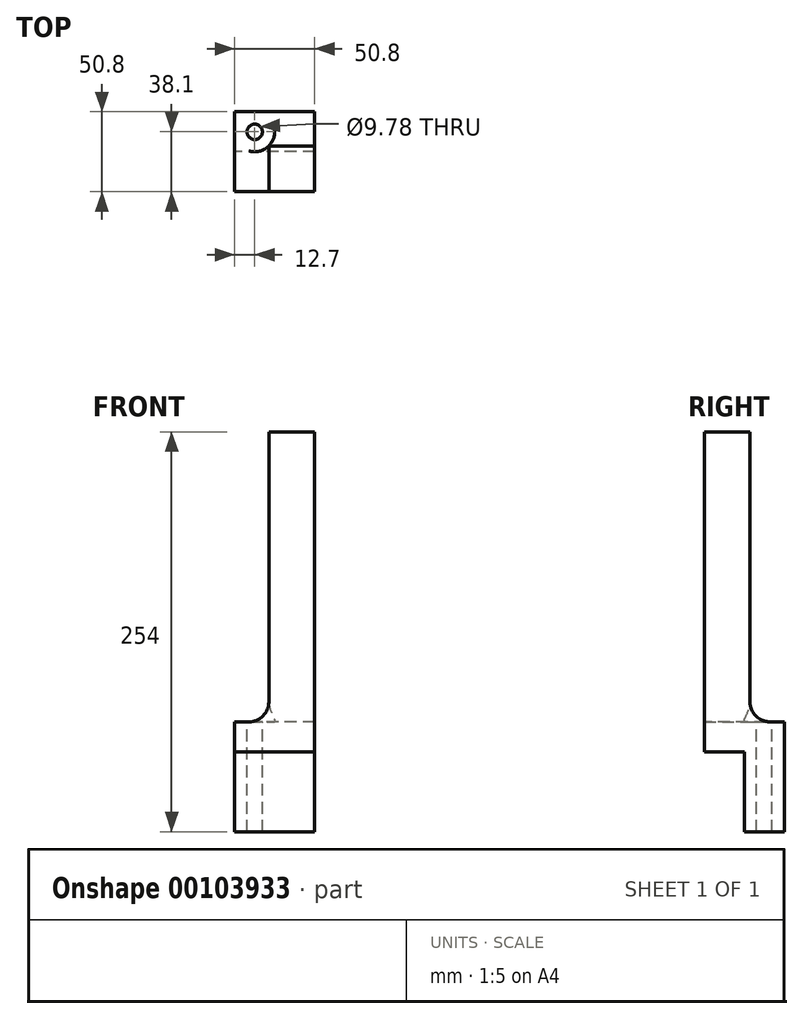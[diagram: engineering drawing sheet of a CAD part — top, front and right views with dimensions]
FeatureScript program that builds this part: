
annotation { "Feature Type Name" : "Feature", "Feature Type Description" : "" }
export const myFeature = defineFeature(function(context is Context, id is Id, definition is map)
    precondition{}
    {
        {
            var Q0;
            Q0=qCreatedBy(makeId("Top.planeOp"),FACE);
            var sketch = newSketch(context, id + "F0", { "sketchPlane" : qUnion([Q0])});
            skLineSegment(sketch, "E0.bottom", {"start": v(0, 0) * mm, "end": v(-50.8, 0) * mm});
            skLineSegment(sketch, "E0.top", {"start": v(0, 50.8) * mm, "end": v(-50.8, 50.8) * mm});
            skLineSegment(sketch, "E0.left", {"start": v(0, 0) * mm, "end": v(0, 50.8) * mm});
            skLineSegment(sketch, "E0.right", {"start": v(-50.8, 0) * mm, "end": v(-50.8, 50.8) * mm});
            skSolve(sketch);
        }
        {
            var Q0;
            Q0=qSketchRegion(id+"F0",true);
            extrude(context, id + "F1", {"entities" : qUnion([Q0]), "depth" : 254 * mm});
        }
        {
            var Q0;
            Q0=makeQuery(id+"F1.opExtrude","SWEPT_FACE",FACE,{"disambiguationData":[OSD([sQuery(id+"F0.wireOp",EDGE,"E0.right")])]});
            var sketch = newSketch(context, id + "F2", { "sketchPlane" : qUnion([Q0])});
            skLineSegment(sketch, "E1", {"start": v(-50.8, 69.85) * mm, "end": v(-41.82, 69.85) * mm});
            skArc(sketch, "E2", {"start": v(-41.82, 69.85) * mm, "mid": v(-32.84, 73.57) * mm, "end": v(-29.12, 82.55) * mm});
            skLineSegment(sketch, "E3", {"start": v(-29.12, 82.55) * mm, "end": v(-29.12, 254) * mm});
            skLineSegment(sketch, "E4", {"start": v(-29.12, 254) * mm, "end": v(-50.8, 254) * mm});
            skLineSegment(sketch, "E5", {"start": v(-50.8, 254) * mm, "end": v(-50.8, 69.85) * mm});
            skSolve(sketch);
        }
        {
            var Q0;
            Q0=qSketchRegion(id+"F2",true);
            extrude(context, id + "F3", {"entities" : qUnion([Q0]), "operationType" : NewBodyOperationType.REMOVE, "endBound" : BoundingType.THROUGH_ALL, "oppositeDirection" : true, "depth" : 25.4 * mm});
        }
        {
            var Q0;
            Q0=makeQuery(id+"F1.opExtrude","SWEPT_FACE",FACE,{"disambiguationData":[OSD([sQuery(id+"F0.wireOp",EDGE,"E0.top")])]});
            var sketch = newSketch(context, id + "F4", { "sketchPlane" : qUnion([Q0])});
            skLineSegment(sketch, "E6", {"start": v(41.82, 69.85) * mm, "end": v(50.8, 69.85) * mm});
            skLineSegment(sketch, "E7", {"start": v(50.8, 69.85) * mm, "end": v(50.8, 254) * mm});
            skLineSegment(sketch, "E8", {"start": v(50.8, 254) * mm, "end": v(29.12, 254) * mm});
            skLineSegment(sketch, "E9", {"start": v(29.12, 254) * mm, "end": v(29.12, 82.55) * mm});
            skArc(sketch, "E10", {"start": v(29.12, 82.55) * mm, "mid": v(32.84, 73.57) * mm, "end": v(41.82, 69.85) * mm});
            skSolve(sketch);
        }
        {
            var Q0;
            Q0=qSketchRegion(id+"F4",true);
            extrude(context, id + "F5", {"entities" : qUnion([Q0]), "operationType" : NewBodyOperationType.REMOVE, "endBound" : BoundingType.THROUGH_ALL, "oppositeDirection" : true, "depth" : 25.4 * mm});
        }
        {
            var Q0;
            Q0=makeQuery(id+"F5.boolean.opBoolean","MERGE",FACE,{"derivedFrom":[makeQuery(id+"F3.boolean.opBoolean","COPY",FACE,{"derivedFrom":makeQuery(id+"F3.opExtrude","SWEPT_FACE",FACE,{"disambiguationData":[OSD([sQuery(id+"F2.wireOp",EDGE,"E1")])]})}),makeQuery(id+"F5.opExtrude","SWEPT_FACE",FACE,{"disambiguationData":[OSD([sQuery(id+"F4.wireOp",EDGE,"E6")])]})]});
            var sketch = newSketch(context, id + "F6", { "sketchPlane" : qUnion([Q0])});
            skCircle(sketch, "E11", {"center": v(-38.1, 38.1) * mm, "radius": 12.7 * mm});
            skSolve(sketch);
        }
        {
            var Q0;
            Q0=qSketchRegion(id+"F6",true);
            extrude(context, id + "F7", {"entities" : qUnion([Q0]), "operationType" : NewBodyOperationType.REMOVE, "depth" : 25.4 * mm});
        }
        {
            var Q0;
            Q0=makeQuery(id+"F1.opExtrude","SWEPT_FACE",FACE,{"disambiguationData":[OSD([sQuery(id+"F0.wireOp",EDGE,"E0.right")])]});
            var sketch = newSketch(context, id + "F8", { "sketchPlane" : qUnion([Q0])});
            skLineSegment(sketch, "E12.bottom", {"start": v(0, 0) * mm, "end": v(-25.4, 0) * mm});
            skLineSegment(sketch, "E12.top", {"start": v(0, 50.8) * mm, "end": v(-25.4, 50.8) * mm});
            skLineSegment(sketch, "E12.left", {"start": v(0, 0) * mm, "end": v(0, 50.8) * mm});
            skLineSegment(sketch, "E12.right", {"start": v(-25.4, 0) * mm, "end": v(-25.4, 50.8) * mm});
            skSolve(sketch);
        }
        {
            var Q0;
            Q0=qSketchRegion(id+"F8",true);
            extrude(context, id + "F9", {"entities" : qUnion([Q0]), "operationType" : NewBodyOperationType.REMOVE, "endBound" : BoundingType.THROUGH_ALL, "oppositeDirection" : true, "depth" : 76.2 * mm});
        }
        {
            var Q0;
            Q0=makeQuery(id+"F7.boolean.opBoolean","MERGE",FACE,{"derivedFrom":[makeQuery(id+"F5.boolean.opBoolean","MERGE",FACE,{"derivedFrom":[makeQuery(id+"F3.boolean.opBoolean","COPY",FACE,{"derivedFrom":makeQuery(id+"F3.opExtrude","SWEPT_FACE",FACE,{"disambiguationData":[OSD([sQuery(id+"F2.wireOp",EDGE,"E1")])]})}),makeQuery(id+"F5.opExtrude","SWEPT_FACE",FACE,{"disambiguationData":[OSD([sQuery(id+"F4.wireOp",EDGE,"E6")])]})]}),makeQuery(id+"F7.opExtrude","CAP_FACE",FACE,{"disambiguationData":[OSD([sQuery(id+"F6.wireOp",EDGE,"E11")])],"isStart":true})]});
            var sketch = newSketch(context, id + "F10", { "sketchPlane" : qUnion([Q0])});
            skCircle(sketch, "E13", {"center": v(-38.1, 38.1) * mm, "radius": 4.89 * mm});
            skSolve(sketch);
        }
        {
            var Q0;
            Q0 = qSketchRegion(id + "F10", true);
            extrude(context, id + "F11", {"entities" : qUnion([Q0]), "operationType" : NewBodyOperationType.REMOVE, "endBound" : BoundingType.THROUGH_ALL, "oppositeDirection" : true, "depth" : 25.4 * mm});
        }
    });
